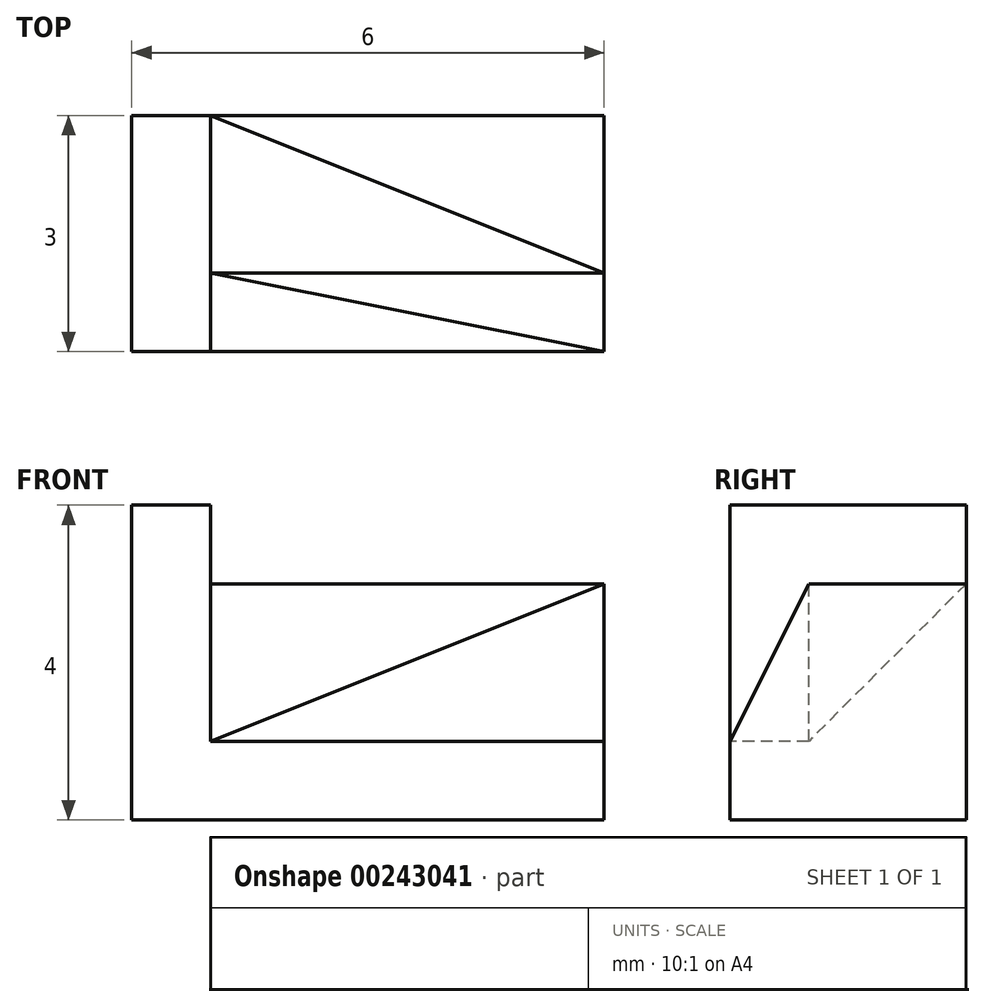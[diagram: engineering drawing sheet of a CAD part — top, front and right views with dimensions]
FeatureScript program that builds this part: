
annotation { "Feature Type Name" : "Feature", "Feature Type Description" : "" }
export const myFeature = defineFeature(function(context is Context, id is Id, definition is map)
    precondition{}
    {
        {
            var Q0;
            Q0=qCreatedBy(makeId("Top.planeOp"),FACE);
            var sketch = newSketch(context, id + "F0", { "sketchPlane" : qUnion([Q0])});
            skLineSegment(sketch, "E0.bottom", {"start": v(0, 0) * mm, "end": v(6, 0) * mm});
            skLineSegment(sketch, "E0.top", {"start": v(0, 3) * mm, "end": v(6, 3) * mm});
            skLineSegment(sketch, "E0.left", {"start": v(0, 0) * mm, "end": v(0, 3) * mm});
            skLineSegment(sketch, "E0.right", {"start": v(6, 0) * mm, "end": v(6, 3) * mm});
            skSolve(sketch);
        }
        {
            var Q0;
            Q0 = qSketchRegion(id + "F0", true);
            extrude(context, id + "F1", {"entities" : qUnion([Q0]), "depth" : 4 * mm});
        }
        {
            var Q0;
            Q0=makeQuery(id+"F1.opExtrude","CAP_FACE",FACE,{"disambiguationData":[OSD([sQuery(id+"F0.wireOp",EDGE,"E0.bottom"),sQuery(id+"F0.wireOp",EDGE,"E0.top"),sQuery(id+"F0.wireOp",EDGE,"E0.left"),sQuery(id+"F0.wireOp",EDGE,"E0.right")])],"isStart":false});
            var sketch = newSketch(context, id + "F2", { "sketchPlane" : qUnion([Q0])});
            skLineSegment(sketch, "E1.bottom", {"start": v(1, 3) * mm, "end": v(6, 3) * mm});
            skLineSegment(sketch, "E1.top", {"start": v(1, 0) * mm, "end": v(6, 0) * mm});
            skLineSegment(sketch, "E1.left", {"start": v(1, 3) * mm, "end": v(1, 0) * mm});
            skLineSegment(sketch, "E1.right", {"start": v(6, 3) * mm, "end": v(6, 0) * mm});
            skSolve(sketch);
        }
        {
            var Q0;
            Q0=makeQuery(id+"F2.imprint","IMPRINT",FACE,{"disambiguationData":[TD([[makeQuery(id+"F2.imprint","IMPRINT",EDGE,{"derivedFrom":sQuery(id+"F2.wireOp",EDGE,"E1.bottom")}),-1.0]])]});
            extrude(context, id + "F3", {"entities" : qUnion([Q0]), "operationType" : NewBodyOperationType.REMOVE, "oppositeDirection" : true, "depth" : 1 * mm});
        }
        {
            var Q0;
            Q0=makeQuery(id+"F3.boolean.opBoolean","COPY",FACE,{"derivedFrom":makeQuery(id+"F3.opExtrude","CAP_FACE",FACE,{"disambiguationData":[OSD([sQuery(id+"F2.wireOp",EDGE,"E1.bottom"),sQuery(id+"F2.wireOp",EDGE,"E1.top"),sQuery(id+"F2.wireOp",EDGE,"E1.left"),sQuery(id+"F2.wireOp",EDGE,"E1.right")])],"isStart":false})});
            var sketch = newSketch(context, id + "F4", { "sketchPlane" : qUnion([Q0])});
            skLineSegment(sketch, "E2.bottom", {"start": v(1, 0) * mm, "end": v(6, 0) * mm});
            skLineSegment(sketch, "E2.top", {"start": v(1, 1) * mm, "end": v(6, 1) * mm});
            skLineSegment(sketch, "E2.left", {"start": v(1, 0) * mm, "end": v(1, 1) * mm});
            skLineSegment(sketch, "E2.right", {"start": v(6, 0) * mm, "end": v(6, 1) * mm});
            skSolve(sketch);
        }
        {
            var Q0;
            Q0=makeQuery(id+"F4.imprint","IMPRINT",FACE,{"disambiguationData":[TD([[makeQuery(id+"F4.imprint","IMPRINT",EDGE,{"derivedFrom":sQuery(id+"F4.wireOp",EDGE,"E2.bottom")}),1.0]])]});
            extrude(context, id + "F5", {"entities" : qUnion([Q0]), "operationType" : NewBodyOperationType.REMOVE, "oppositeDirection" : true, "depth" : 2 * mm});
        }
        {
            var Q0;
            Q0=makeQuery(id+"F3.boolean.opBoolean","COPY",VERTEX,{"derivedFrom":makeQuery(id+"F3.opExtrude","CAP_VERTEX",VERTEX,{"disambiguationData":[OSD([sQuery(id+"F0.wireOp",EDGE,"E0.top"),sQuery(id+"F2.wireOp",EDGE,"E1.bottom"),sQuery(id+"F2.wireOp",EDGE,"E1.left")])],"isStart":false})});
            var Q1;
            Q1=makeQuery(id+"F5.boolean.opBoolean","COPY",VERTEX,{"derivedFrom":makeQuery(id+"F5.opExtrude","CAP_VERTEX",VERTEX,{"disambiguationData":[OSD([sQuery(id+"F2.wireOp",EDGE,"E1.right"),sQuery(id+"F4.wireOp",EDGE,"E2.top"),sQuery(id+"F4.wireOp",EDGE,"E2.right")])],"isStart":true})});
            var Q2;
            Q2=makeQuery(id+"F5.boolean.opBoolean","COPY",VERTEX,{"derivedFrom":makeQuery(id+"F5.opExtrude","CAP_VERTEX",VERTEX,{"disambiguationData":[OSD([sQuery(id+"F2.wireOp",EDGE,"E1.left"),sQuery(id+"F4.wireOp",EDGE,"E2.top"),sQuery(id+"F4.wireOp",EDGE,"E2.left")])],"isStart":false})});
            cPlane(context, id + "F6", {"entities" : qUnion([Q0, Q1, Q2]), "cplaneType" : CPlaneType.THREE_POINT, "offset" : 25 * mm, "width" : 150 * mm, "height" : 150 * mm});
        }
        {
            var Q0;
            Q0=qCreatedBy(id+"F6.planeOp",FACE);
            var sketch = newSketch(context, id + "F7", { "sketchPlane" : qUnion([Q0])});
            skPoint(sketch, "E3.0", {"position": v(0.96, 4.24) * mm});
            skPoint(sketch, "E4.0", {"position": v(0.96, 1.41) * mm});
            skPoint(sketch, "E5.0", {"position": v(6.16, 2.83) * mm});
            skLineSegment(sketch, "E6", {"start": v(0.96, 4.24) * mm, "end": v(6.16, 2.83) * mm});
            skLineSegment(sketch, "E7", {"start": v(6.16, 2.83) * mm, "end": v(0.96, 1.41) * mm});
            skLineSegment(sketch, "E8", {"start": v(0.96, 4.24) * mm, "end": v(0.96, 1.41) * mm});
            skSolve(sketch);
        }
        {
            var Q0;
            Q0=sQuery(id+"F7.wireOp",VERTEX,"E4.0");
            var Q1;
            Q1=makeQuery(id+"F5.boolean.opBoolean","COPY",VERTEX,{"derivedFrom":makeQuery(id+"F5.opExtrude","CAP_VERTEX",VERTEX,{"disambiguationData":[OSD([sQuery(id+"F4.wireOp",EDGE,"E2.bottom"),sQuery(id+"F4.wireOp",EDGE,"E2.right")])],"isStart":false})});
            var Q2;
            Q2=sQuery(id+"F7.wireOp",VERTEX,"E5.0");
            cPlane(context, id + "F8", {"entities" : qUnion([Q0, Q1, Q2]), "cplaneType" : CPlaneType.THREE_POINT, "offset" : 25 * mm, "width" : 150 * mm, "height" : 150 * mm});
        }
        {
            var Q0;
            Q0=qCreatedBy(id+"F8.planeOp",FACE);
            var sketch = newSketch(context, id + "F9", { "sketchPlane" : qUnion([Q0])});
            skPoint(sketch, "E9.0", {"position": v(-0.9, 1.34) * mm});
            skPoint(sketch, "E10.0", {"position": v(-5.98, 0.9) * mm});
            skPoint(sketch, "E11.0", {"position": v(-5.98, 3.13) * mm});
            skLineSegment(sketch, "E12", {"start": v(-0.9, 1.34) * mm, "end": v(-5.98, 0.9) * mm});
            skLineSegment(sketch, "E13", {"start": v(-5.98, 3.13) * mm, "end": v(-5.98, 0.9) * mm});
            skLineSegment(sketch, "E14", {"start": v(-0.9, 1.34) * mm, "end": v(-5.98, 3.13) * mm});
            skSolve(sketch);
        }
        {
            var Q0;
            Q0 = qSketchRegion(id + "F9", true);
            extrude(context, id + "F10", {"entities" : qUnion([Q0]), "operationType" : NewBodyOperationType.ADD, "depth" : 1 * mm});
        }
        {
            var Q0;
            Q0=makeQuery(id+"F1.opExtrude","SWEPT_FACE",FACE,{"disambiguationData":[OSD([sQuery(id+"F0.wireOp",EDGE,"E0.right")])]});
            var sketch = newSketch(context, id + "F11", { "sketchPlane" : qUnion([Q0])});
            skLineSegment(sketch, "E15.bottom", {"start": v(0, 0) * mm, "end": v(3, 0) * mm});
            skLineSegment(sketch, "E15.top", {"start": v(0, 3) * mm, "end": v(3, 3) * mm});
            skLineSegment(sketch, "E15.left", {"start": v(0, 0) * mm, "end": v(0, 3) * mm});
            skLineSegment(sketch, "E15.right", {"start": v(3, 0) * mm, "end": v(3, 3) * mm});
            skSolve(sketch);
        }
        {
            var Q0;
            Q0 = qSketchRegion(id + "F11", true);
            extrude(context, id + "F12", {"entities" : qUnion([Q0]), "operationType" : NewBodyOperationType.REMOVE, "depth" : 25 * mm});
        }
        {
            var Q0;
            Q0 = qSketchRegion(id + "F7", true);
            extrude(context, id + "F13", {"entities" : qUnion([Q0]), "operationType" : NewBodyOperationType.REMOVE, "depth" : 1 * mm});
        }
        {
            var Q0;
            Q0=makeQuery(id+"F5.boolean.opBoolean","MERGE",FACE,{"derivedFrom":[makeQuery(id+"F3.boolean.opBoolean","COPY",FACE,{"derivedFrom":makeQuery(id+"F3.opExtrude","SWEPT_FACE",FACE,{"disambiguationData":[OSD([sQuery(id+"F2.wireOp",EDGE,"E1.left")])]})}),makeQuery(id+"F5.opExtrude","SWEPT_FACE",FACE,{"disambiguationData":[OSD([sQuery(id+"F4.wireOp",EDGE,"E2.left")])]})]});
            var sketch = newSketch(context, id + "F14", { "sketchPlane" : qUnion([Q0])});
            skLineSegment(sketch, "E16.bottom", {"start": v(0, 1) * mm, "end": v(3, 1) * mm});
            skLineSegment(sketch, "E16.top", {"start": v(0, 4) * mm, "end": v(3, 4) * mm});
            skLineSegment(sketch, "E16.left", {"start": v(0, 1) * mm, "end": v(0, 4) * mm});
            skLineSegment(sketch, "E16.right", {"start": v(3, 1) * mm, "end": v(3, 4) * mm});
            skPoint(sketch, "E17.oppositeSnap0", {"position": v(1.87, 3.34) * mm});
            skSolve(sketch);
        }
        {
            var Q0;
            Q0 = qSketchRegion(id + "F14", true);
            extrude(context, id + "F15", {"entities" : qUnion([Q0]), "operationType" : NewBodyOperationType.ADD, "oppositeDirection" : true, "depth" : 1 * mm});
        }
        {
            var Q0;
            Q0=makeQuery(id+"F15.boolean.opBoolean","MERGE",FACE,{"derivedFrom":[makeQuery(id+"F5.boolean.opBoolean","MERGE",FACE,{"derivedFrom":[makeQuery(id+"F3.boolean.opBoolean","COPY",FACE,{"derivedFrom":makeQuery(id+"F3.opExtrude","SWEPT_FACE",FACE,{"disambiguationData":[OSD([sQuery(id+"F2.wireOp",EDGE,"E1.left")])]})}),makeQuery(id+"F5.opExtrude","SWEPT_FACE",FACE,{"disambiguationData":[OSD([sQuery(id+"F4.wireOp",EDGE,"E2.left")])]})]}),makeQuery(id+"F15.opExtrude","CAP_FACE",FACE,{"disambiguationData":[OSD([sQuery(id+"F14.wireOp",EDGE,"E16.bottom"),sQuery(id+"F14.wireOp",EDGE,"E16.top"),sQuery(id+"F14.wireOp",EDGE,"E16.left"),sQuery(id+"F14.wireOp",EDGE,"E16.right")])],"isStart":true})]});
            var sketch = newSketch(context, id + "F16", { "sketchPlane" : qUnion([Q0])});
            skLineSegment(sketch, "E18.bottom", {"start": v(1, 2.47) * mm, "end": v(1.53, 2.47) * mm});
            skLineSegment(sketch, "E18.top", {"start": v(1, 3) * mm, "end": v(1.53, 3) * mm});
            skLineSegment(sketch, "E18.left", {"start": v(1, 2.47) * mm, "end": v(1, 3) * mm});
            skLineSegment(sketch, "E18.right", {"start": v(1.53, 2.47) * mm, "end": v(1.53, 3) * mm});
            skSolve(sketch);
        }
        {
            var Q0;
            Q0 = qSketchRegion(id + "F16", true);
            extrude(context, id + "F17", {"entities" : qUnion([Q0]), "operationType" : NewBodyOperationType.REMOVE, "depth" : 1.4 * mm});
        }
    });
